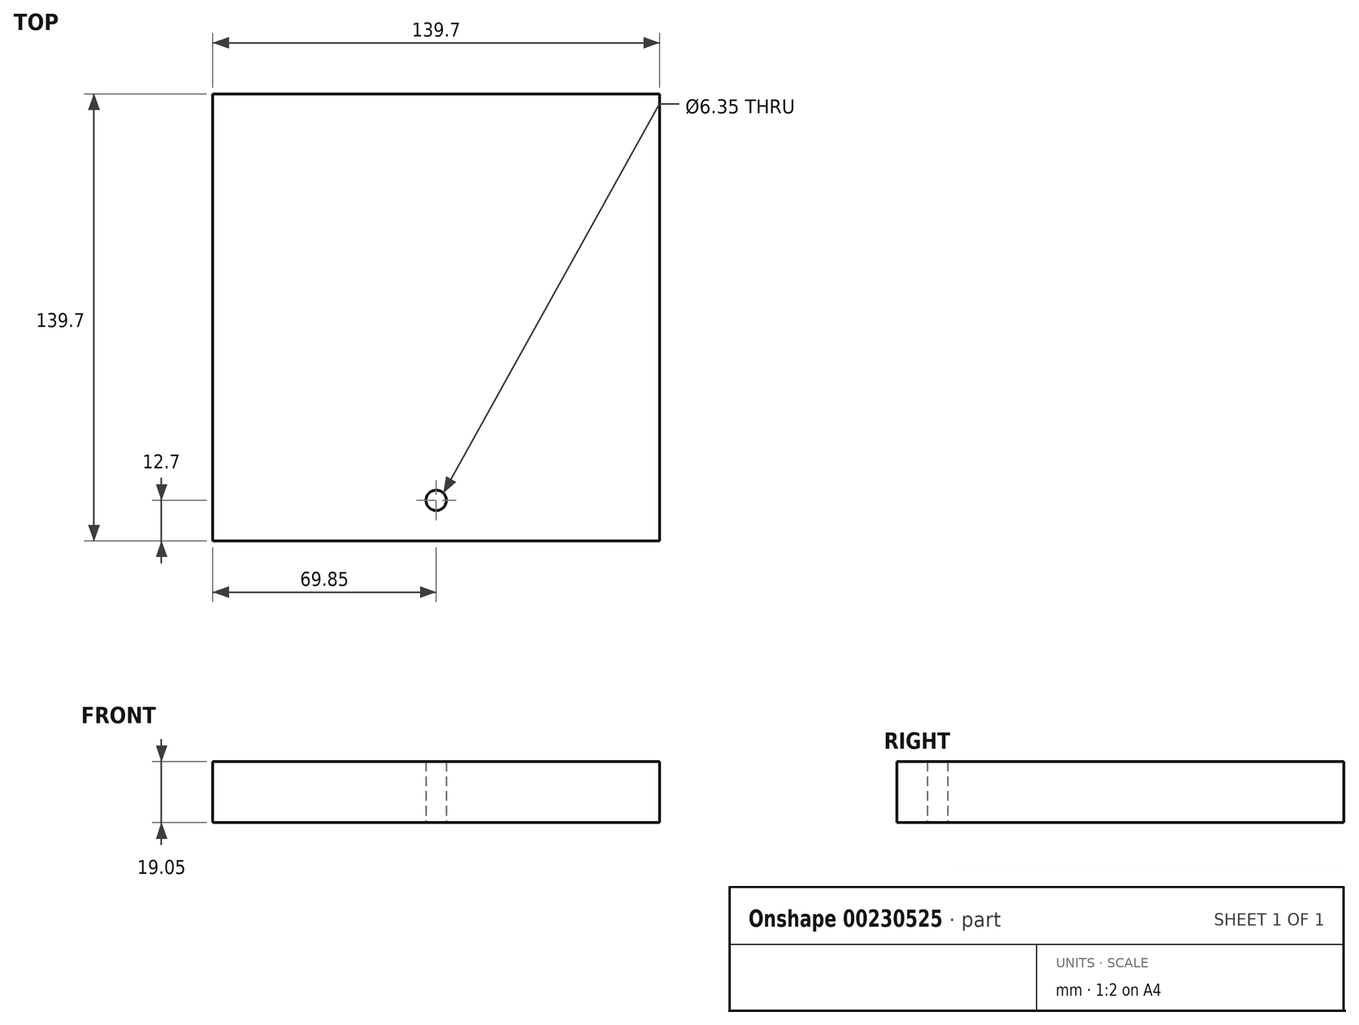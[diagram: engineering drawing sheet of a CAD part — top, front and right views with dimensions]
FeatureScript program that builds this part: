
annotation { "Feature Type Name" : "Feature", "Feature Type Description" : "" }
export const myFeature = defineFeature(function(context is Context, id is Id, definition is map)
    precondition{}
    {
        {
            var Q0;
            Q0=qCreatedBy(makeId("Top.planeOp"),FACE);
            var sketch = newSketch(context, id + "F0", { "sketchPlane" : qUnion([Q0])});
            skLineSegment(sketch, "E0.bottom", {"start": v(-69.85, 69.85) * mm, "end": v(69.85, 69.85) * mm});
            skLineSegment(sketch, "E0.top", {"start": v(-69.85, -69.85) * mm, "end": v(69.85, -69.85) * mm});
            skLineSegment(sketch, "E0.left", {"start": v(-69.85, 69.85) * mm, "end": v(-69.85, -69.85) * mm});
            skLineSegment(sketch, "E0.right", {"start": v(69.85, 69.85) * mm, "end": v(69.85, -69.85) * mm});
            skPoint(sketch, "E0.middle", {"position": v(0, 0) * mm});
            skLineSegment(sketch, "E1", {"start": v(0, -69.85) * mm, "end": v(0, -57.15) * mm});
            skPoint(sketch, "E1.endSnap0", {"position": v(0, -69.85) * mm});
            skCircle(sketch, "E2", {"center": v(0, -57.15) * mm, "radius": 3.18 * mm});
            skSolve(sketch);
        }
        {
            var Q0;
            Q0=makeQuery(id+"F0.imprint","IMPRINT",FACE,{"disambiguationData":[TD([[makeQuery(id+"F0.imprint","IMPRINT",EDGE,{"derivedFrom":sQuery(id+"F0.wireOp",EDGE,"E0.bottom")}),-1.0]])]});
            extrude(context, id + "F1", {"entities" : qUnion([Q0]), "depth" : 19.05 * mm});
        }
    });
